# Revit family: FAHB 2 WIDE (HORIZONTAL FAN)
name_source: partatom
category: Mechanical Equipment
units: mm (PartAtom-declared; Revit-internal decimal feet)

## family parameters
Always vertical = Yes
Classification = None
Cut with Voids When Loaded = No
OmniClass Number = 23.75.00.00
OmniClass Title = Climate Control (HVAC)
Part Type = Normal
Room Calculation Point = No
Round Connector Dimension = Use Diameter
Shared = No
Work Plane-Based = No

## types (6) — shared parameters
Copper Pipes = Copper Pipe
Description = FLUID COOLERS FEVB WITH HORIZONTAL FLOW
Fan001 = Yes
Fan002 = Yes
Full Load Amps (FLA) = Amps-1
Full load Amps (FLA)-2 = Amps-2
Inlet Pipe Size = 2"
Inlet Pipe Size (Radius) = 1.06 "
Manufacturer = HUSSMANN CORPORATION
Outlet Pipe Size = 2"
Outlet Pipe Size (Radius) = 1"
Overall Height = 87.62 "
Phase = 3
TEXT = 1 "
Type Comments = Systems
Voltage = 460 V
Voltage - 2 = 208 V

## per-type parameters (varying)
| type | Fan003 | Fan004 | Fan005 | Fan006 | Fan007 | Model | Revit Family Dates | URL | Unit Width |
| FAHB 2 X 2 | No | No | No | No | No | FEHB 2 X2 | 08/17/2023 HM |  | 76.28 " |
| FAHB 2 X 3 | Yes | No | No | No | No | FAHB 2 X 3 | 08/17/2023 HM |  | 112.68 " |
| FAHB 2 X 4 | Yes | Yes | No | No | No | FAHB 2 X 4 | 08/17/2023 HM |  | 148 " |
| FAHB 2 X 5 | Yes | Yes | Yes | No | No | FAHB 2 X 5 | 08/17/2023 HM |  | 184.28 " |
| FAHB 2 X 6 | Yes | Yes | Yes | Yes | No | FAHB 2 X 6 | 08/17/2023 HM |  | 220.28 " |
| FAHB 2 X 7 | Yes | Yes | Yes | Yes | Yes | FAHB 2 X 7 | 09/06/2023HM | hussmann.com | 256.28 " |

## geometry (parser evidence)
native form markers: Sweep x12
no freeform markers — native parametric forms only
